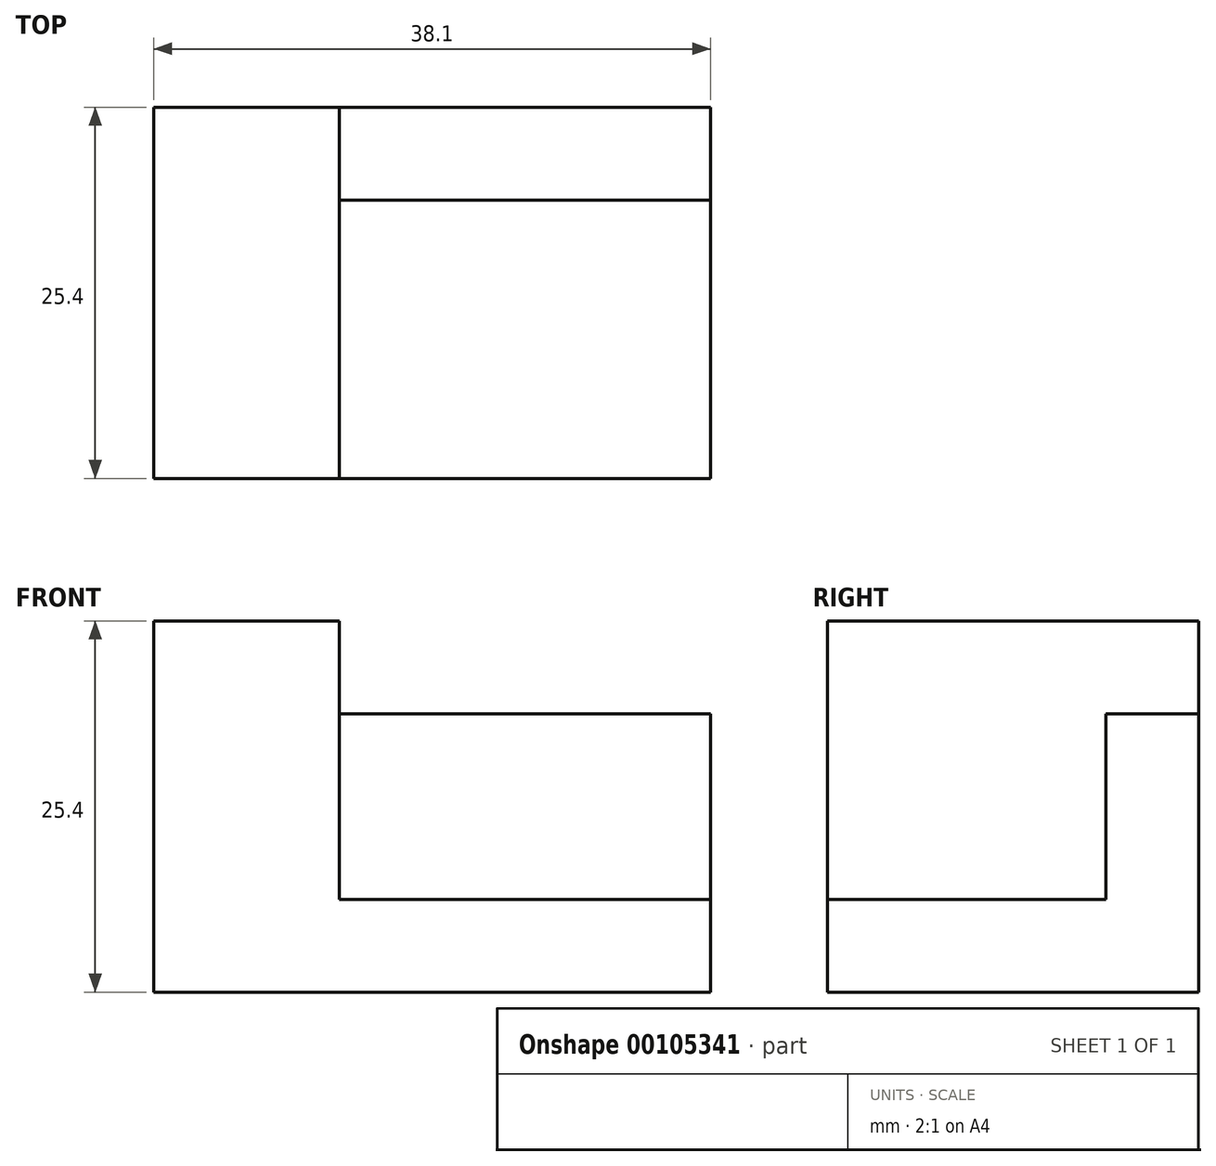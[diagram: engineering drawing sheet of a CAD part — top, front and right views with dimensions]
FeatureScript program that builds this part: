
annotation { "Feature Type Name" : "Feature", "Feature Type Description" : "" }
export const myFeature = defineFeature(function(context is Context, id is Id, definition is map)
    precondition{}
    {
        {
            var Q0;
            Q0=qCreatedBy(makeId("Front.planeOp"),FACE);
            var sketch = newSketch(context, id + "F0", { "sketchPlane" : qUnion([Q0])});
            skLineSegment(sketch, "E0.bottom", {"start": v(0, 0) * mm, "end": v(38.1, 0) * mm});
            skLineSegment(sketch, "E0.top", {"start": v(0, 25.4) * mm, "end": v(38.1, 25.4) * mm});
            skLineSegment(sketch, "E0.left", {"start": v(0, 0) * mm, "end": v(0, 25.4) * mm});
            skLineSegment(sketch, "E0.right", {"start": v(38.1, 0) * mm, "end": v(38.1, 25.4) * mm});
            skSolve(sketch);
        }
        {
            var Q0;
            Q0 = qSketchRegion(id + "F0", true);
            extrude(context, id + "F1", {"entities" : qUnion([Q0]), "endBound" : BoundingType.SYMMETRIC, "depth" : 25.4 * mm});
        }
        {
            var Q0;
            Q0=qCreatedBy(makeId("Front.planeOp"),FACE);
            var sketch = newSketch(context, id + "F2", { "sketchPlane" : qUnion([Q0])});
            skLineSegment(sketch, "E1.bottom", {"start": v(38.1, 25.4) * mm, "end": v(12.7, 25.4) * mm});
            skLineSegment(sketch, "E1.top", {"start": v(38.1, 19.05) * mm, "end": v(12.7, 19.05) * mm});
            skLineSegment(sketch, "E1.left", {"start": v(38.1, 25.4) * mm, "end": v(38.1, 19.05) * mm});
            skLineSegment(sketch, "E1.right", {"start": v(12.7, 25.4) * mm, "end": v(12.7, 19.05) * mm});
            skSolve(sketch);
        }
        {
            var Q0;
            Q0 = qSketchRegion(id + "F2", true);
            extrude(context, id + "F3", {"entities" : qUnion([Q0]), "operationType" : NewBodyOperationType.REMOVE, "endBound" : BoundingType.SYMMETRIC, "oppositeDirection" : true, "depth" : 101.6 * mm});
        }
        {
            var Q0;
            Q0=qCreatedBy(makeId("Front.planeOp"),FACE);
            var sketch = newSketch(context, id + "F4", { "sketchPlane" : qUnion([Q0])});
            skLineSegment(sketch, "E2.bottom", {"start": v(12.7, 19.05) * mm, "end": v(38.1, 19.05) * mm});
            skLineSegment(sketch, "E2.top", {"start": v(12.7, 6.35) * mm, "end": v(38.1, 6.35) * mm});
            skLineSegment(sketch, "E2.left", {"start": v(12.7, 19.05) * mm, "end": v(12.7, 6.35) * mm});
            skLineSegment(sketch, "E2.right", {"start": v(38.1, 19.05) * mm, "end": v(38.1, 6.35) * mm});
            skSolve(sketch);
        }
        {
            var Q0;
            Q0 = qSketchRegion(id + "F4", true);
            extrude(context, id + "F5", {"entities" : qUnion([Q0]), "operationType" : NewBodyOperationType.REMOVE, "depth" : 35.08 * mm, "hasSecondDirection" : true, "secondDirectionOppositeDirection" : true, "secondDirectionDepth" : 6.35 * mm});
        }
    });
